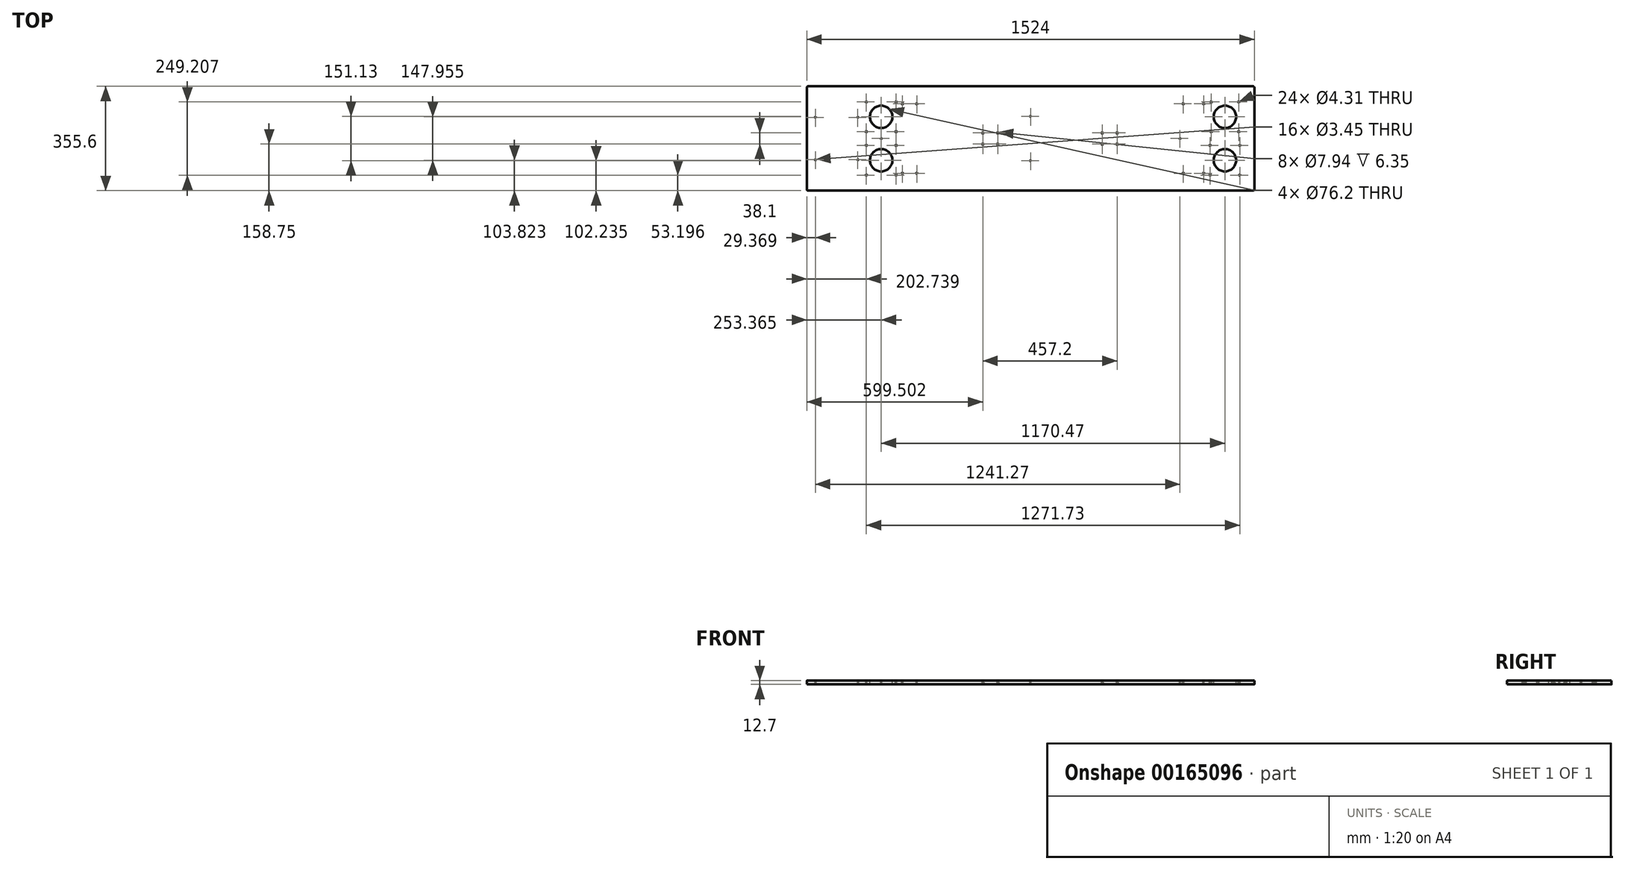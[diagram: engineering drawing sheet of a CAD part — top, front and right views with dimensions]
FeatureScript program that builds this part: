
annotation { "Feature Type Name" : "Feature", "Feature Type Description" : "" }
export const myFeature = defineFeature(function(context is Context, id is Id, definition is map)
    precondition{}
    {
        {
            var Q0;
            Q0=qCreatedBy(makeId("Top.planeOp"),FACE);
            var sketch = newSketch(context, id + "F0", { "sketchPlane" : qUnion([Q0])});
            skLineSegment(sketch, "E0", {"start": v(0, 0) * mm, "end": v(0, -177.8) * mm});
            skLineSegment(sketch, "E1", {"start": v(0, 0) * mm, "end": v(0, 177.8) * mm});
            skLineSegment(sketch, "E2", {"start": v(0, 177.8) * mm, "end": v(-1524, 177.8) * mm});
            skLineSegment(sketch, "E3", {"start": v(-1524, 177.8) * mm, "end": v(-1524, -177.8) * mm});
            skLineSegment(sketch, "E4", {"start": v(-1524, -177.8) * mm, "end": v(0, -177.8) * mm});
            skLineSegment(sketch, "E5", {"start": v(-304.8, 0) * mm, "end": v(-304.8, 304.8) * mm, "construction": true});
            skLineSegment(sketch, "E6.bottom", {"start": v(-457.2, 254) * mm, "end": v(-152.4, 254) * mm, "construction": true});
            skLineSegment(sketch, "E6.top", {"start": v(-457.2, 355.6) * mm, "end": v(-152.4, 355.6) * mm, "construction": true});
            skLineSegment(sketch, "E6.left", {"start": v(-457.2, 254) * mm, "end": v(-457.2, 355.6) * mm, "construction": true});
            skLineSegment(sketch, "E6.right", {"start": v(-152.4, 254) * mm, "end": v(-152.4, 355.6) * mm, "construction": true});
            skPoint(sketch, "E6.middle", {"position": v(-304.8, 304.8) * mm});
            skLineSegment(sketch, "E7", {"start": v(0, 0) * mm, "end": v(-304.8, 0) * mm, "construction": true});
            skLineSegment(sketch, "E8", {"start": v(-1524, 0) * mm, "end": v(-1422.4, 0) * mm, "construction": true});
            skLineSegment(sketch, "E9.bottom", {"start": v(-1494.63, -72.23) * mm, "end": v(-1350.17, -72.23) * mm, "construction": true});
            skLineSegment(sketch, "E9.top", {"start": v(-1494.63, 72.23) * mm, "end": v(-1350.17, 72.23) * mm, "construction": true});
            skLineSegment(sketch, "E9.left", {"start": v(-1494.63, -72.23) * mm, "end": v(-1494.63, 72.23) * mm, "construction": true});
            skLineSegment(sketch, "E9.right", {"start": v(-1350.17, -72.23) * mm, "end": v(-1350.17, 72.23) * mm, "construction": true});
            skPoint(sketch, "E9.middle", {"position": v(-1422.4, 0) * mm});
            skCircle(sketch, "E10", {"center": v(-1350.17, 72.23) * mm, "radius": 1.73 * mm});
            skCircle(sketch, "E11", {"center": v(-1494.63, 72.23) * mm, "radius": 1.73 * mm});
            skCircle(sketch, "E12", {"center": v(-1494.63, -72.23) * mm, "radius": 1.73 * mm});
            skCircle(sketch, "E13", {"center": v(-1350.17, -72.23) * mm, "radius": 1.73 * mm});
            skSolve(sketch);
        }
        {
            var Q0;
            Q0=makeQuery(id+"F0.imprint","IMPRINT",FACE,{"disambiguationData":[TD([[makeQuery(id+"F0.imprint","IMPRINT",EDGE,{"derivedFrom":sQuery(id+"F0.wireOp",EDGE,"J4rKfvQ3-Jgxj-aFfy-9oJb-s6s6XNZOLIcy")}),-1.0]])]});
            var Q1;
            Q1=makeQuery(id+"F0.imprint","IMPRINT",FACE,{"disambiguationData":[TD([[makeQuery(id+"F0.imprint","IMPRINT",EDGE,{"derivedFrom":sQuery(id+"F0.wireOp",EDGE,"E0")}),-1.0]])]});
            extrude(context, id + "F1", {"entities" : qUnion([Q0, Q1]), "depth" : 12.7 * mm});
        }
        {
            var Q0;
            Q0=makeQuery(id+"F1.opExtrude","CAP_FACE",FACE,{"disambiguationData":[OSD([sQuery(id+"F0.wireOp",EDGE,"J4rKfvQ3-Jgxj-aFfy-9oJb-s6s6XNZOLIcy"),sQuery(id+"F0.wireOp",EDGE,"Xf2MZohT-rgO5-9ukW-ZWbA-0kJiTxAe4SJI"),sQuery(id+"F0.wireOp",EDGE,"lEohr3j7-oXLC-NFWG-A5Xo-WYQsRyGbpgG9"),sQuery(id+"F0.wireOp",EDGE,"3uYUpdRW-uV09-m1ik-G79e-Kg7JKOHa71x2"),sQuery(id+"F0.wireOp",EDGE,"fRVqIEsL-uzPl-mkAL-NF8B-gKytSxVZeo2V"),sQuery(id+"F0.wireOp",EDGE,"jUA6iyPq-aLYq-uZWl-Ht5r-vboFaG9r1abN"),sQuery(id+"F0.wireOp",EDGE,"E2"),sQuery(id+"F0.wireOp",EDGE,"E3"),sQuery(id+"F0.wireOp",EDGE,"E4")])],"isStart":false});
            var sketch = newSketch(context, id + "F2", { "sketchPlane" : qUnion([Q0])});
            skLineSegment(sketch, "E14", {"start": v(-253.37, 0) * mm, "end": v(-762, 0) * mm, "construction": true});
            skLineSegment(sketch, "E15", {"start": v(-762, 0) * mm, "end": v(-1270.64, 0) * mm, "construction": true});
            skLineSegment(sketch, "E16", {"start": v(-1270.64, 0) * mm, "end": v(-1524, 0) * mm, "construction": true});
            skLineSegment(sketch, "E17", {"start": v(-762, 177.8) * mm, "end": v(-762, -75.57) * mm, "construction": true});
            skLineSegment(sketch, "E18", {"start": v(-762, 75.57) * mm, "end": v(-762, -75.57) * mm, "construction": true});
            skLineSegment(sketch, "E19", {"start": v(-762, 75.57) * mm, "end": v(-762, -177.8) * mm, "construction": true});
            skCircle(sketch, "E20", {"center": v(-1270.64, 0) * mm, "radius": 1.73 * mm});
            skCircle(sketch, "E21", {"center": v(-762, -75.57) * mm, "radius": 1.73 * mm});
            skCircle(sketch, "E22", {"center": v(-762, 75.57) * mm, "radius": 1.73 * mm});
            skCircle(sketch, "E23", {"center": v(-253.37, 0) * mm, "radius": 1.73 * mm});
            skPoint(sketch, "E24.middle", {"position": v(-762, 0) * mm});
            skCircle(sketch, "E25", {"center": v(-100.16, 73.98) * mm, "radius": 38.1 * mm});
            skCircle(sketch, "E26", {"center": v(-100.16, -73.98) * mm, "radius": 38.1 * mm});
            skCircle(sketch, "E27", {"center": v(-1270.64, 73.98) * mm, "radius": 38.1 * mm});
            skCircle(sketch, "E28", {"center": v(-1270.64, -73.98) * mm, "radius": 38.1 * mm});
            skLineSegment(sketch, "E29.bottom", {"start": v(-147.13, 124.6) * mm, "end": v(-53.2, 124.6) * mm, "construction": true});
            skLineSegment(sketch, "E29.top", {"start": v(-147.13, 23.35) * mm, "end": v(-53.2, 23.35) * mm, "construction": true});
            skLineSegment(sketch, "E29.left", {"start": v(-147.13, 124.6) * mm, "end": v(-147.13, 23.35) * mm, "construction": true});
            skLineSegment(sketch, "E29.right", {"start": v(-53.2, 124.6) * mm, "end": v(-53.2, 23.35) * mm, "construction": true});
            skLineSegment(sketch, "E30.bottom", {"start": v(-150.79, -124.6) * mm, "end": v(-49.54, -124.6) * mm, "construction": true});
            skLineSegment(sketch, "E30.top", {"start": v(-150.79, -23.35) * mm, "end": v(-49.54, -23.35) * mm, "construction": true});
            skLineSegment(sketch, "E30.left", {"start": v(-150.79, -124.6) * mm, "end": v(-150.79, -23.35) * mm, "construction": true});
            skLineSegment(sketch, "E30.right", {"start": v(-49.54, -124.6) * mm, "end": v(-49.54, -23.35) * mm, "construction": true});
            skLineSegment(sketch, "E31.bottom", {"start": v(-1321.26, 124.6) * mm, "end": v(-1220, 124.6) * mm, "construction": true});
            skLineSegment(sketch, "E31.top", {"start": v(-1321.26, 23.35) * mm, "end": v(-1220, 23.35) * mm, "construction": true});
            skLineSegment(sketch, "E31.left", {"start": v(-1321.26, 124.6) * mm, "end": v(-1321.26, 23.35) * mm, "construction": true});
            skLineSegment(sketch, "E31.right", {"start": v(-1220, 124.6) * mm, "end": v(-1220, 23.35) * mm, "construction": true});
            skLineSegment(sketch, "E32.bottom", {"start": v(-1321.26, -124.6) * mm, "end": v(-1220, -124.6) * mm, "construction": true});
            skLineSegment(sketch, "E32.top", {"start": v(-1321.26, -23.35) * mm, "end": v(-1220, -23.35) * mm, "construction": true});
            skLineSegment(sketch, "E32.left", {"start": v(-1321.26, -124.6) * mm, "end": v(-1321.26, -23.35) * mm, "construction": true});
            skLineSegment(sketch, "E32.right", {"start": v(-1220, -124.6) * mm, "end": v(-1220, -23.35) * mm, "construction": true});
            skCircle(sketch, "E33", {"center": v(-150.79, -124.6) * mm, "radius": 2.15 * mm});
            skCircle(sketch, "E34", {"center": v(-49.54, -124.6) * mm, "radius": 2.15 * mm});
            skCircle(sketch, "E35", {"center": v(-49.54, -23.35) * mm, "radius": 2.15 * mm});
            skCircle(sketch, "E36", {"center": v(-150.79, -23.35) * mm, "radius": 2.15 * mm});
            skCircle(sketch, "E37", {"center": v(-147.13, 23.35) * mm, "radius": 2.15 * mm});
            skCircle(sketch, "E38", {"center": v(-147.13, 124.6) * mm, "radius": 2.15 * mm});
            skCircle(sketch, "E39", {"center": v(-53.2, 124.6) * mm, "radius": 2.15 * mm});
            skCircle(sketch, "E40", {"center": v(-53.2, 124.6) * mm, "radius": 3.97 * mm, "construction": true});
            skCircle(sketch, "E41", {"center": v(-1270.64, 73.98) * mm, "radius": 75.57 * mm, "construction": true});
            skLineSegment(sketch, "E42.bottom", {"start": v(-1494.63, 72.23) * mm, "end": v(-1350.17, 72.23) * mm, "construction": true});
            skLineSegment(sketch, "E42.top", {"start": v(-1494.63, -72.23) * mm, "end": v(-1350.17, -72.23) * mm, "construction": true});
            skLineSegment(sketch, "E42.left", {"start": v(-1494.63, 72.23) * mm, "end": v(-1494.63, -72.23) * mm, "construction": true});
            skLineSegment(sketch, "E42.right", {"start": v(-1350.17, 72.23) * mm, "end": v(-1350.17, -72.23) * mm, "construction": true});
            skPoint(sketch, "E42.middle", {"position": v(-1422.4, 0) * mm});
            skCircle(sketch, "E43", {"center": v(-1350.17, 72.23) * mm, "radius": 3.97 * mm, "construction": true});
            skLineSegment(sketch, "E44", {"start": v(-1346.2, 72.23) * mm, "end": v(-1346.2, 0) * mm, "construction": true});
            skCircle(sketch, "E45", {"center": v(-53.2, 23.35) * mm, "radius": 2.15 * mm});
            skCircle(sketch, "E46", {"center": v(-1321.26, -124.6) * mm, "radius": 2.15 * mm});
            skCircle(sketch, "E47", {"center": v(-1220, -124.6) * mm, "radius": 2.15 * mm});
            skCircle(sketch, "E48", {"center": v(-1220, -23.35) * mm, "radius": 2.15 * mm});
            skCircle(sketch, "E49", {"center": v(-1321.26, -23.35) * mm, "radius": 2.15 * mm});
            skCircle(sketch, "E50", {"center": v(-1321.26, 23.35) * mm, "radius": 2.15 * mm});
            skCircle(sketch, "E51", {"center": v(-1220, 23.35) * mm, "radius": 2.15 * mm});
            skCircle(sketch, "E52", {"center": v(-1220, 124.6) * mm, "radius": 2.15 * mm});
            skCircle(sketch, "E53", {"center": v(-1321.26, 124.6) * mm, "radius": 2.15 * mm});
            skLineSegment(sketch, "E54.right", {"start": v(-1270.64, 73.98) * mm, "end": v(-1270.64, -73.98) * mm, "construction": true});
            skLineSegment(sketch, "E55", {"start": v(-49.54, -73.98) * mm, "end": v(-150.79, -73.98) * mm, "construction": true});
            skLineSegment(sketch, "E56", {"start": v(-53.2, 73.98) * mm, "end": v(-147.13, 73.98) * mm, "construction": true});
            skLineSegment(sketch, "E57", {"start": v(0, 177.8) * mm, "end": v(0, 152.4) * mm, "construction": true});
            skCircle(sketch, "E58", {"center": v(-100.16, 73.98) * mm, "radius": 73.03 * mm, "construction": true});
            skLineSegment(sketch, "E59", {"start": v(-100.16, 73.98) * mm, "end": v(-100.16, -73.98) * mm, "construction": true});
            skCircle(sketch, "E60", {"center": v(-1321.26, 124.6) * mm, "radius": 3.97 * mm, "construction": true});
            skPoint(sketch, "E61", {"position": v(-100.16, 0) * mm});
            skLineSegment(sketch, "E62", {"start": v(0, 0) * mm, "end": v(0, -1701.8) * mm, "construction": true});
            skLineSegment(sketch, "E63", {"start": v(0, -1701.8) * mm, "end": v(-1524, -1701.8) * mm, "construction": true});
            skLineSegment(sketch, "E64", {"start": v(-1524, -1701.8) * mm, "end": v(-1524, -177.8) * mm, "construction": true});
            skLineSegment(sketch, "E65", {"start": v(-762, -177.8) * mm, "end": v(-762, -1701.8) * mm, "construction": true});
            skLineSegment(sketch, "E66", {"start": v(-100.16, 124.6) * mm, "end": v(-100.16, 177.8) * mm, "construction": true});
            skLineSegment(sketch, "E67", {"start": v(-53.2, 73.98) * mm, "end": v(0, 73.98) * mm, "construction": true});
            skSolve(sketch);
        }
        {
            var Q0;
            Q0=qSketchRegion(id+"F2",true);
            var Q1;
            Q1=makeQuery(id+"F1.opExtrude","CAP_FACE",FACE,{"disambiguationData":[OSD([sQuery(id+"F0.wireOp",EDGE,"J4rKfvQ3-Jgxj-aFfy-9oJb-s6s6XNZOLIcy"),sQuery(id+"F0.wireOp",EDGE,"Xf2MZohT-rgO5-9ukW-ZWbA-0kJiTxAe4SJI"),sQuery(id+"F0.wireOp",EDGE,"lEohr3j7-oXLC-NFWG-A5Xo-WYQsRyGbpgG9"),sQuery(id+"F0.wireOp",EDGE,"3uYUpdRW-uV09-m1ik-G79e-Kg7JKOHa71x2"),sQuery(id+"F0.wireOp",EDGE,"fRVqIEsL-uzPl-mkAL-NF8B-gKytSxVZeo2V"),sQuery(id+"F0.wireOp",EDGE,"jUA6iyPq-aLYq-uZWl-Ht5r-vboFaG9r1abN"),sQuery(id+"F0.wireOp",EDGE,"E2"),sQuery(id+"F0.wireOp",EDGE,"E3"),sQuery(id+"F0.wireOp",EDGE,"E4")])],"isStart":true});
            extrude(context, id + "F3", {"entities" : qUnion([Q0]), "operationType" : NewBodyOperationType.REMOVE, "endBound" : BoundingType.UP_TO_SURFACE, "oppositeDirection" : true, "endBoundEntityFace" : qUnion([Q1]), "depth" : 25.4 * mm});
        }
        {
            var Q0;
            Q0=makeQuery(id+"F1.opExtrude","CAP_FACE",FACE,{"disambiguationData":[OSD([sQuery(id+"F0.wireOp",EDGE,"J4rKfvQ3-Jgxj-aFfy-9oJb-s6s6XNZOLIcy"),sQuery(id+"F0.wireOp",EDGE,"Xf2MZohT-rgO5-9ukW-ZWbA-0kJiTxAe4SJI"),sQuery(id+"F0.wireOp",EDGE,"lEohr3j7-oXLC-NFWG-A5Xo-WYQsRyGbpgG9"),sQuery(id+"F0.wireOp",EDGE,"3uYUpdRW-uV09-m1ik-G79e-Kg7JKOHa71x2"),sQuery(id+"F0.wireOp",EDGE,"fRVqIEsL-uzPl-mkAL-NF8B-gKytSxVZeo2V"),sQuery(id+"F0.wireOp",EDGE,"jUA6iyPq-aLYq-uZWl-Ht5r-vboFaG9r1abN"),sQuery(id+"F0.wireOp",EDGE,"E2"),sQuery(id+"F0.wireOp",EDGE,"E3"),sQuery(id+"F0.wireOp",EDGE,"E4")])],"isStart":false});
            var sketch = newSketch(context, id + "F4", { "sketchPlane" : qUnion([Q0])});
            skPoint(sketch, "E68.middle", {"position": v(-695.9, 0) * mm});
            skLineSegment(sketch, "E69", {"start": v(-492.7, 0) * mm, "end": v(-899.1, 0) * mm, "construction": true});
            skLineSegment(sketch, "E70.bottom", {"start": v(-467.3, 19.05) * mm, "end": v(-518.1, 19.05) * mm, "construction": true});
            skLineSegment(sketch, "E70.top", {"start": v(-467.3, -19.05) * mm, "end": v(-518.1, -19.05) * mm, "construction": true});
            skLineSegment(sketch, "E70.left", {"start": v(-467.3, 19.05) * mm, "end": v(-467.3, -19.05) * mm, "construction": true});
            skLineSegment(sketch, "E70.right", {"start": v(-518.1, 19.05) * mm, "end": v(-518.1, -19.05) * mm, "construction": true});
            skPoint(sketch, "E70.middle", {"position": v(-492.7, 0) * mm});
            skLineSegment(sketch, "E71.bottom", {"start": v(-873.7, -19.05) * mm, "end": v(-924.5, -19.05) * mm, "construction": true});
            skLineSegment(sketch, "E71.top", {"start": v(-873.7, 19.05) * mm, "end": v(-924.5, 19.05) * mm, "construction": true});
            skLineSegment(sketch, "E71.left", {"start": v(-873.7, -19.05) * mm, "end": v(-873.7, 19.05) * mm, "construction": true});
            skLineSegment(sketch, "E71.right", {"start": v(-924.5, -19.05) * mm, "end": v(-924.5, 19.05) * mm, "construction": true});
            skPoint(sketch, "E71.middle", {"position": v(-899.1, 0) * mm});
            skCircle(sketch, "E72", {"center": v(-467.3, -19.05) * mm, "radius": 1.73 * mm});
            skCircle(sketch, "E73", {"center": v(-518.1, -19.05) * mm, "radius": 1.73 * mm});
            skCircle(sketch, "E74", {"center": v(-518.1, 19.05) * mm, "radius": 1.73 * mm});
            skCircle(sketch, "E75", {"center": v(-467.3, 19.05) * mm, "radius": 1.73 * mm});
            skCircle(sketch, "E76", {"center": v(-873.7, 19.05) * mm, "radius": 1.73 * mm});
            skCircle(sketch, "E77", {"center": v(-873.7, -19.05) * mm, "radius": 1.73 * mm});
            skCircle(sketch, "E78", {"center": v(-924.5, -19.05) * mm, "radius": 1.73 * mm});
            skCircle(sketch, "E79", {"center": v(-924.5, 19.05) * mm, "radius": 1.73 * mm});
            skLineSegment(sketch, "E80.bottom", {"start": v(-242.29, -118.37) * mm, "end": v(-172.55, -118.37) * mm, "construction": true});
            skLineSegment(sketch, "E80.top", {"start": v(-242.29, 118.37) * mm, "end": v(-172.55, 118.37) * mm, "construction": true});
            skLineSegment(sketch, "E80.left", {"start": v(-242.29, -118.37) * mm, "end": v(-242.29, 118.37) * mm, "construction": true});
            skLineSegment(sketch, "E80.right", {"start": v(-172.55, -118.37) * mm, "end": v(-172.55, 118.37) * mm, "construction": true});
            skPoint(sketch, "E80.middle", {"position": v(-207.42, 0) * mm});
            skCircle(sketch, "E81", {"center": v(-172.55, 118.37) * mm, "radius": 2.15 * mm});
            skCircle(sketch, "E82", {"center": v(-242.29, 118.37) * mm, "radius": 2.15 * mm});
            skCircle(sketch, "E83", {"center": v(-242.29, -118.37) * mm, "radius": 2.15 * mm});
            skCircle(sketch, "E84", {"center": v(-172.55, -118.37) * mm, "radius": 2.15 * mm});
            skLineSegment(sketch, "E85.bottom", {"start": v(-1149.5, -118.37) * mm, "end": v(-1198.25, -118.37) * mm, "construction": true});
            skLineSegment(sketch, "E85.top", {"start": v(-1149.5, 118.37) * mm, "end": v(-1198.25, 118.37) * mm, "construction": true});
            skLineSegment(sketch, "E85.left", {"start": v(-1149.5, -118.37) * mm, "end": v(-1149.5, 118.37) * mm, "construction": true});
            skLineSegment(sketch, "E85.right", {"start": v(-1198.25, -118.37) * mm, "end": v(-1198.25, 118.37) * mm, "construction": true});
            skPoint(sketch, "E85.middle", {"position": v(-1173.88, 0) * mm});
            skCircle(sketch, "E86", {"center": v(-100.16, -73.98) * mm, "radius": 72.4 * mm, "construction": true});
            skCircle(sketch, "E87", {"center": v(-1270.64, -73.98) * mm, "radius": 72.4 * mm, "construction": true});
            skCircle(sketch, "E88", {"center": v(-1198.25, -118.37) * mm, "radius": 2.15 * mm});
            skCircle(sketch, "E89", {"center": v(-1149.5, -118.37) * mm, "radius": 2.15 * mm});
            skCircle(sketch, "E90", {"center": v(-1198.25, 118.37) * mm, "radius": 2.15 * mm});
            skCircle(sketch, "E91", {"center": v(-1149.5, 118.37) * mm, "radius": 2.15 * mm});
            skLineSegment(sketch, "E92", {"start": v(-1149.5, 0) * mm, "end": v(-899.1, 0) * mm, "construction": true});
            skLineSegment(sketch, "E93", {"start": v(-242.29, 0) * mm, "end": v(-492.7, 0) * mm, "construction": true});
            skSolve(sketch);
        }
        {
            var Q0;
            Q0=qSketchRegion(id+"F4",true);
            var Q1;
            Q1=makeQuery(id+"F1.opExtrude","CAP_FACE",FACE,{"disambiguationData":[OSD([sQuery(id+"F0.wireOp",EDGE,"J4rKfvQ3-Jgxj-aFfy-9oJb-s6s6XNZOLIcy"),sQuery(id+"F0.wireOp",EDGE,"Xf2MZohT-rgO5-9ukW-ZWbA-0kJiTxAe4SJI"),sQuery(id+"F0.wireOp",EDGE,"lEohr3j7-oXLC-NFWG-A5Xo-WYQsRyGbpgG9"),sQuery(id+"F0.wireOp",EDGE,"3uYUpdRW-uV09-m1ik-G79e-Kg7JKOHa71x2"),sQuery(id+"F0.wireOp",EDGE,"fRVqIEsL-uzPl-mkAL-NF8B-gKytSxVZeo2V"),sQuery(id+"F0.wireOp",EDGE,"jUA6iyPq-aLYq-uZWl-Ht5r-vboFaG9r1abN"),sQuery(id+"F0.wireOp",EDGE,"E2"),sQuery(id+"F0.wireOp",EDGE,"E3"),sQuery(id+"F0.wireOp",EDGE,"E4")])],"isStart":true});
            extrude(context, id + "F5", {"entities" : qUnion([Q0]), "operationType" : NewBodyOperationType.REMOVE, "endBound" : BoundingType.UP_TO_SURFACE, "oppositeDirection" : true, "endBoundEntityFace" : qUnion([Q1]), "depth" : 25.4 * mm});
        }
        {
            var Q0;
            Q0=makeQuery(id+"F1.opExtrude","CAP_FACE",FACE,{"disambiguationData":[OSD([sQuery(id+"F0.wireOp",EDGE,"J4rKfvQ3-Jgxj-aFfy-9oJb-s6s6XNZOLIcy"),sQuery(id+"F0.wireOp",EDGE,"Xf2MZohT-rgO5-9ukW-ZWbA-0kJiTxAe4SJI"),sQuery(id+"F0.wireOp",EDGE,"lEohr3j7-oXLC-NFWG-A5Xo-WYQsRyGbpgG9"),sQuery(id+"F0.wireOp",EDGE,"3uYUpdRW-uV09-m1ik-G79e-Kg7JKOHa71x2"),sQuery(id+"F0.wireOp",EDGE,"fRVqIEsL-uzPl-mkAL-NF8B-gKytSxVZeo2V"),sQuery(id+"F0.wireOp",EDGE,"jUA6iyPq-aLYq-uZWl-Ht5r-vboFaG9r1abN"),sQuery(id+"F0.wireOp",EDGE,"E2"),sQuery(id+"F0.wireOp",EDGE,"E3"),sQuery(id+"F0.wireOp",EDGE,"E4"),sQuery(id+"F0.wireOp",EDGE,"E10"),sQuery(id+"F0.wireOp",EDGE,"E11"),sQuery(id+"F0.wireOp",EDGE,"E12"),sQuery(id+"F0.wireOp",EDGE,"E13")])],"isStart":true});
            var sketch = newSketch(context, id + "F6", { "sketchPlane" : qUnion([Q0])});
            skCircle(sketch, "E94", {"center": v(-924.5, -19.05) * mm, "radius": 3.97 * mm});
            skCircle(sketch, "E95", {"center": v(-873.7, -19.05) * mm, "radius": 3.97 * mm});
            skCircle(sketch, "E96", {"center": v(-873.7, 19.05) * mm, "radius": 3.97 * mm});
            skCircle(sketch, "E97", {"center": v(-924.5, 19.05) * mm, "radius": 3.97 * mm});
            skCircle(sketch, "E98", {"center": v(-467.3, -19.05) * mm, "radius": 3.97 * mm});
            skCircle(sketch, "E99", {"center": v(-467.3, 19.05) * mm, "radius": 3.97 * mm});
            skCircle(sketch, "E100", {"center": v(-518.1, 19.05) * mm, "radius": 3.97 * mm});
            skCircle(sketch, "E101", {"center": v(-518.1, -19.05) * mm, "radius": 3.97 * mm});
            skSolve(sketch);
        }
        {
            var Q0;
            Q0=qSketchRegion(id+"F6",true);
            extrude(context, id + "F7", {"entities" : qUnion([Q0]), "operationType" : NewBodyOperationType.REMOVE, "oppositeDirection" : true, "depth" : 6.35 * mm});
        }
        {
            var Q0;
            Q0=makeQuery(id+"F1.opExtrude","SWEPT_EDGE",EDGE,{"disambiguationData":[OSD([sQuery(id+"F0.wireOp",EDGE,"jUA6iyPq-aLYq-uZWl-Ht5r-vboFaG9r1abN"),sQuery(id+"F0.wireOp",EDGE,"E4")])]});
            var Q1;
            Q1=makeQuery(id+"F1.opExtrude","SWEPT_EDGE",EDGE,{"disambiguationData":[OSD([sQuery(id+"F0.wireOp",EDGE,"fRVqIEsL-uzPl-mkAL-NF8B-gKytSxVZeo2V"),sQuery(id+"F0.wireOp",EDGE,"jUA6iyPq-aLYq-uZWl-Ht5r-vboFaG9r1abN")])]});
            var Q2;
            Q2=makeQuery(id+"F1.opExtrude","SWEPT_EDGE",EDGE,{"disambiguationData":[OSD([sQuery(id+"F0.wireOp",EDGE,"3uYUpdRW-uV09-m1ik-G79e-Kg7JKOHa71x2"),sQuery(id+"F0.wireOp",EDGE,"fRVqIEsL-uzPl-mkAL-NF8B-gKytSxVZeo2V")])]});
            var Q3;
            Q3=makeQuery(id+"F1.opExtrude","SWEPT_EDGE",EDGE,{"disambiguationData":[OSD([sQuery(id+"F0.wireOp",EDGE,"lEohr3j7-oXLC-NFWG-A5Xo-WYQsRyGbpgG9"),sQuery(id+"F0.wireOp",EDGE,"3uYUpdRW-uV09-m1ik-G79e-Kg7JKOHa71x2")])]});
            var Q4;
            Q4=makeQuery(id+"F1.opExtrude","SWEPT_EDGE",EDGE,{"disambiguationData":[OSD([sQuery(id+"F0.wireOp",EDGE,"Xf2MZohT-rgO5-9ukW-ZWbA-0kJiTxAe4SJI"),sQuery(id+"F0.wireOp",EDGE,"lEohr3j7-oXLC-NFWG-A5Xo-WYQsRyGbpgG9")])]});
            var Q5;
            Q5=makeQuery(id+"F1.opExtrude","SWEPT_EDGE",EDGE,{"disambiguationData":[OSD([sQuery(id+"F0.wireOp",EDGE,"J4rKfvQ3-Jgxj-aFfy-9oJb-s6s6XNZOLIcy"),sQuery(id+"F0.wireOp",EDGE,"Xf2MZohT-rgO5-9ukW-ZWbA-0kJiTxAe4SJI")])]});
            var Q6;
            Q6=makeQuery(id+"F1.opExtrude","SWEPT_EDGE",EDGE,{"disambiguationData":[OSD([sQuery(id+"F0.wireOp",EDGE,"J4rKfvQ3-Jgxj-aFfy-9oJb-s6s6XNZOLIcy"),sQuery(id+"F0.wireOp",EDGE,"E2")])]});
            var Q7;
            Q7=makeQuery(id+"F1.opExtrude","SWEPT_EDGE",EDGE,{"disambiguationData":[OSD([sQuery(id+"F0.wireOp",EDGE,"E2"),sQuery(id+"F0.wireOp",EDGE,"E3")])]});
            var Q8;
            Q8=makeQuery(id+"F1.opExtrude","SWEPT_EDGE",EDGE,{"disambiguationData":[OSD([sQuery(id+"F0.wireOp",EDGE,"E3"),sQuery(id+"F0.wireOp",EDGE,"E4")])]});
            fillet(context, id + "F8", {"entities" : qUnion([Q0, Q1, Q2, Q3, Q4, Q5, Q6, Q7, Q8]), "radius" : 3.97 * mm, "tangentPropagation" : true, "allowEdgeOverflow" : false});
        }
    });
